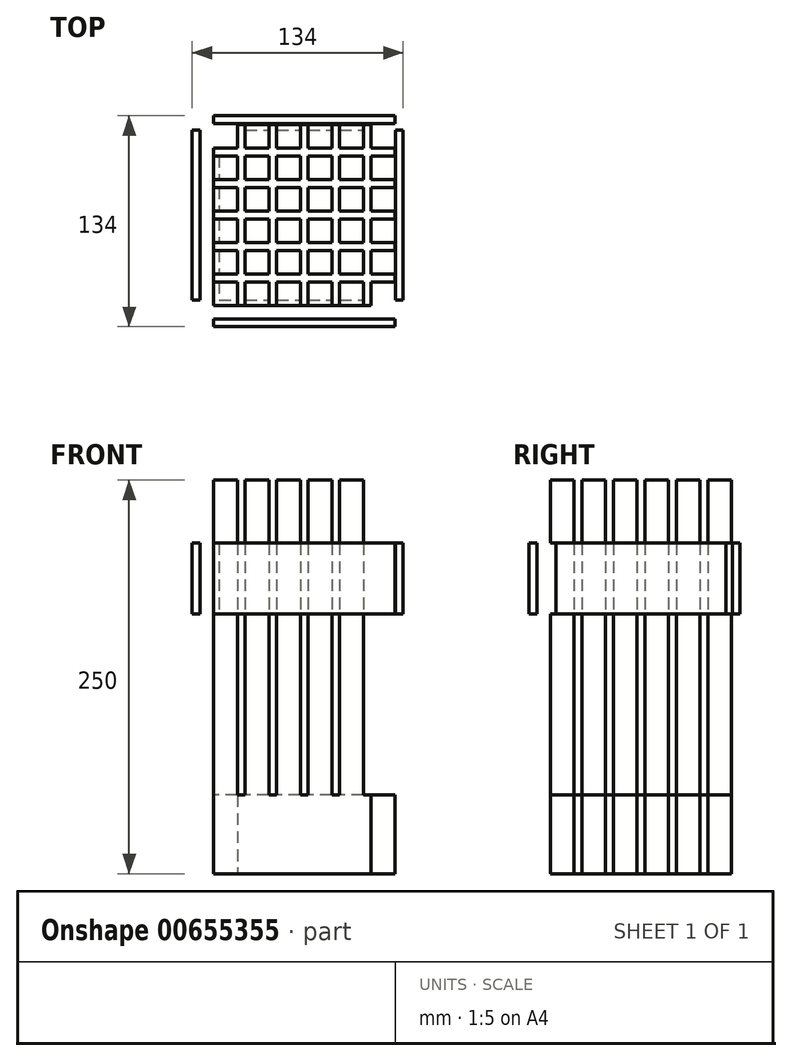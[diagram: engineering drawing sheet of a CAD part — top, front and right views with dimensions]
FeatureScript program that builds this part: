
annotation { "Feature Type Name" : "Feature", "Feature Type Description" : "" }
export const myFeature = defineFeature(function(context is Context, id is Id, definition is map)
    precondition{}
    {
        {
            var Q0;
            Q0=qCreatedBy(makeId("Top.planeOp"),FACE);
            var sketch = newSketch(context, id + "F0", { "sketchPlane" : qUnion([Q0])});
            skLineSegment(sketch, "E0.bottom", {"start": v(-53.36, 61.51) * mm, "end": v(61.64, 61.51) * mm});
            skLineSegment(sketch, "E0.top", {"start": v(-53.36, -53.49) * mm, "end": v(61.64, -53.49) * mm});
            skLineSegment(sketch, "E0.left", {"start": v(-53.36, 61.51) * mm, "end": v(-53.36, -53.49) * mm});
            skLineSegment(sketch, "E0.right", {"start": v(61.64, 61.51) * mm, "end": v(61.64, -53.49) * mm});
            skLineSegment(sketch, "E1.bottom", {"start": v(-53.36, 61.51) * mm, "end": v(-38.36, 61.51) * mm});
            skLineSegment(sketch, "E1.top", {"start": v(-53.36, 46.51) * mm, "end": v(-38.36, 46.51) * mm});
            skLineSegment(sketch, "E1.left", {"start": v(-53.36, 61.51) * mm, "end": v(-53.36, 46.51) * mm});
            skLineSegment(sketch, "E1.right", {"start": v(-38.36, 61.51) * mm, "end": v(-38.36, 46.51) * mm});
            skLineSegment(sketch, "E2.0.1.0", {"start": v(-38.36, 41.51) * mm, "end": v(-38.36, 26.51) * mm});
            skLineSegment(sketch, "E2.0.1.1", {"start": v(-53.36, 26.51) * mm, "end": v(-38.36, 26.51) * mm});
            skLineSegment(sketch, "E2.0.1.2", {"start": v(-53.36, 41.51) * mm, "end": v(-53.36, 26.51) * mm});
            skLineSegment(sketch, "E2.0.1.3", {"start": v(-53.36, 41.51) * mm, "end": v(-38.36, 41.51) * mm});
            skLineSegment(sketch, "E2.0.2.0", {"start": v(-38.36, 21.51) * mm, "end": v(-38.36, 6.51) * mm});
            skLineSegment(sketch, "E2.0.2.1", {"start": v(-53.36, 6.51) * mm, "end": v(-38.36, 6.51) * mm});
            skLineSegment(sketch, "E2.0.2.2", {"start": v(-53.36, 21.51) * mm, "end": v(-53.36, 6.51) * mm});
            skLineSegment(sketch, "E2.0.2.3", {"start": v(-53.36, 21.51) * mm, "end": v(-38.36, 21.51) * mm});
            skLineSegment(sketch, "E2.0.3.0", {"start": v(-38.36, 1.51) * mm, "end": v(-38.36, -13.49) * mm});
            skLineSegment(sketch, "E2.0.3.1", {"start": v(-53.36, -13.49) * mm, "end": v(-38.36, -13.49) * mm});
            skLineSegment(sketch, "E2.0.3.2", {"start": v(-53.36, 1.51) * mm, "end": v(-53.36, -13.49) * mm});
            skLineSegment(sketch, "E2.0.3.3", {"start": v(-53.36, 1.51) * mm, "end": v(-38.36, 1.51) * mm});
            skLineSegment(sketch, "E2.0.4.0", {"start": v(-38.36, -18.49) * mm, "end": v(-38.36, -33.49) * mm});
            skLineSegment(sketch, "E2.0.4.1", {"start": v(-53.36, -33.49) * mm, "end": v(-38.36, -33.49) * mm});
            skLineSegment(sketch, "E2.0.4.2", {"start": v(-53.36, -18.49) * mm, "end": v(-53.36, -33.49) * mm});
            skLineSegment(sketch, "E2.0.4.3", {"start": v(-53.36, -18.49) * mm, "end": v(-38.36, -18.49) * mm});
            skLineSegment(sketch, "E2.0.5.0", {"start": v(-38.36, -38.49) * mm, "end": v(-38.36, -53.49) * mm});
            skLineSegment(sketch, "E2.0.5.1", {"start": v(-53.36, -53.49) * mm, "end": v(-38.36, -53.49) * mm});
            skLineSegment(sketch, "E2.0.5.2", {"start": v(-53.36, -38.49) * mm, "end": v(-53.36, -53.49) * mm});
            skLineSegment(sketch, "E2.0.5.3", {"start": v(-53.36, -38.49) * mm, "end": v(-38.36, -38.49) * mm});
            skLineSegment(sketch, "E2.1.0.0", {"start": v(-18.36, 61.51) * mm, "end": v(-18.36, 46.51) * mm});
            skLineSegment(sketch, "E2.1.0.1", {"start": v(-33.36, 46.51) * mm, "end": v(-18.36, 46.51) * mm});
            skLineSegment(sketch, "E2.1.0.2", {"start": v(-33.36, 61.51) * mm, "end": v(-33.36, 46.51) * mm});
            skLineSegment(sketch, "E2.1.0.3", {"start": v(-33.36, 61.51) * mm, "end": v(-18.36, 61.51) * mm});
            skLineSegment(sketch, "E2.1.1.0", {"start": v(-18.36, 41.51) * mm, "end": v(-18.36, 26.51) * mm});
            skLineSegment(sketch, "E2.1.1.1", {"start": v(-33.36, 26.51) * mm, "end": v(-18.36, 26.51) * mm});
            skLineSegment(sketch, "E2.1.1.2", {"start": v(-33.36, 41.51) * mm, "end": v(-33.36, 26.51) * mm});
            skLineSegment(sketch, "E2.1.1.3", {"start": v(-33.36, 41.51) * mm, "end": v(-18.36, 41.51) * mm});
            skLineSegment(sketch, "E2.1.2.0", {"start": v(-18.36, 21.51) * mm, "end": v(-18.36, 6.51) * mm});
            skLineSegment(sketch, "E2.1.2.1", {"start": v(-33.36, 6.51) * mm, "end": v(-18.36, 6.51) * mm});
            skLineSegment(sketch, "E2.1.2.2", {"start": v(-33.36, 21.51) * mm, "end": v(-33.36, 6.51) * mm});
            skLineSegment(sketch, "E2.1.2.3", {"start": v(-33.36, 21.51) * mm, "end": v(-18.36, 21.51) * mm});
            skLineSegment(sketch, "E2.1.3.0", {"start": v(-18.36, 1.51) * mm, "end": v(-18.36, -13.49) * mm});
            skLineSegment(sketch, "E2.1.3.1", {"start": v(-33.36, -13.49) * mm, "end": v(-18.36, -13.49) * mm});
            skLineSegment(sketch, "E2.1.3.2", {"start": v(-33.36, 1.51) * mm, "end": v(-33.36, -13.49) * mm});
            skLineSegment(sketch, "E2.1.3.3", {"start": v(-33.36, 1.51) * mm, "end": v(-18.36, 1.51) * mm});
            skLineSegment(sketch, "E2.1.4.0", {"start": v(-18.36, -18.49) * mm, "end": v(-18.36, -33.49) * mm});
            skLineSegment(sketch, "E2.1.4.1", {"start": v(-33.36, -33.49) * mm, "end": v(-18.36, -33.49) * mm});
            skLineSegment(sketch, "E2.1.4.2", {"start": v(-33.36, -18.49) * mm, "end": v(-33.36, -33.49) * mm});
            skLineSegment(sketch, "E2.1.4.3", {"start": v(-33.36, -18.49) * mm, "end": v(-18.36, -18.49) * mm});
            skLineSegment(sketch, "E2.1.5.0", {"start": v(-18.36, -38.49) * mm, "end": v(-18.36, -53.49) * mm});
            skLineSegment(sketch, "E2.1.5.1", {"start": v(-33.36, -53.49) * mm, "end": v(-18.36, -53.49) * mm});
            skLineSegment(sketch, "E2.1.5.2", {"start": v(-33.36, -38.49) * mm, "end": v(-33.36, -53.49) * mm});
            skLineSegment(sketch, "E2.1.5.3", {"start": v(-33.36, -38.49) * mm, "end": v(-18.36, -38.49) * mm});
            skLineSegment(sketch, "E2.2.0.0", {"start": v(1.64, 61.51) * mm, "end": v(1.64, 46.51) * mm});
            skLineSegment(sketch, "E2.2.0.1", {"start": v(-13.36, 46.51) * mm, "end": v(1.64, 46.51) * mm});
            skLineSegment(sketch, "E2.2.0.2", {"start": v(-13.36, 61.51) * mm, "end": v(-13.36, 46.51) * mm});
            skLineSegment(sketch, "E2.2.0.3", {"start": v(-13.36, 61.51) * mm, "end": v(1.64, 61.51) * mm});
            skLineSegment(sketch, "E2.2.1.0", {"start": v(1.64, 41.51) * mm, "end": v(1.64, 26.51) * mm});
            skLineSegment(sketch, "E2.2.1.1", {"start": v(-13.36, 26.51) * mm, "end": v(1.64, 26.51) * mm});
            skLineSegment(sketch, "E2.2.1.2", {"start": v(-13.36, 41.51) * mm, "end": v(-13.36, 26.51) * mm});
            skLineSegment(sketch, "E2.2.1.3", {"start": v(-13.36, 41.51) * mm, "end": v(1.64, 41.51) * mm});
            skLineSegment(sketch, "E2.2.2.0", {"start": v(1.64, 21.51) * mm, "end": v(1.64, 6.51) * mm});
            skLineSegment(sketch, "E2.2.2.1", {"start": v(-13.36, 6.51) * mm, "end": v(1.64, 6.51) * mm});
            skLineSegment(sketch, "E2.2.2.2", {"start": v(-13.36, 21.51) * mm, "end": v(-13.36, 6.51) * mm});
            skLineSegment(sketch, "E2.2.2.3", {"start": v(-13.36, 21.51) * mm, "end": v(1.64, 21.51) * mm});
            skLineSegment(sketch, "E2.2.3.0", {"start": v(1.64, 1.51) * mm, "end": v(1.64, -13.49) * mm});
            skLineSegment(sketch, "E2.2.3.1", {"start": v(-13.36, -13.49) * mm, "end": v(1.64, -13.49) * mm});
            skLineSegment(sketch, "E2.2.3.2", {"start": v(-13.36, 1.51) * mm, "end": v(-13.36, -13.49) * mm});
            skLineSegment(sketch, "E2.2.3.3", {"start": v(-13.36, 1.51) * mm, "end": v(1.64, 1.51) * mm});
            skLineSegment(sketch, "E2.2.4.0", {"start": v(1.64, -18.49) * mm, "end": v(1.64, -33.49) * mm});
            skLineSegment(sketch, "E2.2.4.1", {"start": v(-13.36, -33.49) * mm, "end": v(1.64, -33.49) * mm});
            skLineSegment(sketch, "E2.2.4.2", {"start": v(-13.36, -18.49) * mm, "end": v(-13.36, -33.49) * mm});
            skLineSegment(sketch, "E2.2.4.3", {"start": v(-13.36, -18.49) * mm, "end": v(1.64, -18.49) * mm});
            skLineSegment(sketch, "E2.2.5.0", {"start": v(1.64, -38.49) * mm, "end": v(1.64, -53.49) * mm});
            skLineSegment(sketch, "E2.2.5.1", {"start": v(-13.36, -53.49) * mm, "end": v(1.64, -53.49) * mm});
            skLineSegment(sketch, "E2.2.5.2", {"start": v(-13.36, -38.49) * mm, "end": v(-13.36, -53.49) * mm});
            skLineSegment(sketch, "E2.2.5.3", {"start": v(-13.36, -38.49) * mm, "end": v(1.64, -38.49) * mm});
            skLineSegment(sketch, "E2.3.0.0", {"start": v(21.64, 61.51) * mm, "end": v(21.64, 46.51) * mm});
            skLineSegment(sketch, "E2.3.0.1", {"start": v(6.64, 46.51) * mm, "end": v(21.64, 46.51) * mm});
            skLineSegment(sketch, "E2.3.0.2", {"start": v(6.64, 61.51) * mm, "end": v(6.64, 46.51) * mm});
            skLineSegment(sketch, "E2.3.0.3", {"start": v(6.64, 61.51) * mm, "end": v(21.64, 61.51) * mm});
            skLineSegment(sketch, "E2.3.1.0", {"start": v(21.64, 41.51) * mm, "end": v(21.64, 26.51) * mm});
            skLineSegment(sketch, "E2.3.1.1", {"start": v(6.64, 26.51) * mm, "end": v(21.64, 26.51) * mm});
            skLineSegment(sketch, "E2.3.1.2", {"start": v(6.64, 41.51) * mm, "end": v(6.64, 26.51) * mm});
            skLineSegment(sketch, "E2.3.1.3", {"start": v(6.64, 41.51) * mm, "end": v(21.64, 41.51) * mm});
            skLineSegment(sketch, "E2.3.2.0", {"start": v(21.64, 21.51) * mm, "end": v(21.64, 6.51) * mm});
            skLineSegment(sketch, "E2.3.2.1", {"start": v(6.64, 6.51) * mm, "end": v(21.64, 6.51) * mm});
            skLineSegment(sketch, "E2.3.2.2", {"start": v(6.64, 21.51) * mm, "end": v(6.64, 6.51) * mm});
            skLineSegment(sketch, "E2.3.2.3", {"start": v(6.64, 21.51) * mm, "end": v(21.64, 21.51) * mm});
            skLineSegment(sketch, "E2.3.3.0", {"start": v(21.64, 1.51) * mm, "end": v(21.64, -13.49) * mm});
            skLineSegment(sketch, "E2.3.3.1", {"start": v(6.64, -13.49) * mm, "end": v(21.64, -13.49) * mm});
            skLineSegment(sketch, "E2.3.3.2", {"start": v(6.64, 1.51) * mm, "end": v(6.64, -13.49) * mm});
            skLineSegment(sketch, "E2.3.3.3", {"start": v(6.64, 1.51) * mm, "end": v(21.64, 1.51) * mm});
            skLineSegment(sketch, "E2.3.4.0", {"start": v(21.64, -18.49) * mm, "end": v(21.64, -33.49) * mm});
            skLineSegment(sketch, "E2.3.4.1", {"start": v(6.64, -33.49) * mm, "end": v(21.64, -33.49) * mm});
            skLineSegment(sketch, "E2.3.4.2", {"start": v(6.64, -18.49) * mm, "end": v(6.64, -33.49) * mm});
            skLineSegment(sketch, "E2.3.4.3", {"start": v(6.64, -18.49) * mm, "end": v(21.64, -18.49) * mm});
            skLineSegment(sketch, "E2.3.5.0", {"start": v(21.64, -38.49) * mm, "end": v(21.64, -53.49) * mm});
            skLineSegment(sketch, "E2.3.5.1", {"start": v(6.64, -53.49) * mm, "end": v(21.64, -53.49) * mm});
            skLineSegment(sketch, "E2.3.5.2", {"start": v(6.64, -38.49) * mm, "end": v(6.64, -53.49) * mm});
            skLineSegment(sketch, "E2.3.5.3", {"start": v(6.64, -38.49) * mm, "end": v(21.64, -38.49) * mm});
            skLineSegment(sketch, "E2.4.0.0", {"start": v(41.64, 61.51) * mm, "end": v(41.64, 46.51) * mm});
            skLineSegment(sketch, "E2.4.0.1", {"start": v(26.64, 46.51) * mm, "end": v(41.64, 46.51) * mm});
            skLineSegment(sketch, "E2.4.0.2", {"start": v(26.64, 61.51) * mm, "end": v(26.64, 46.51) * mm});
            skLineSegment(sketch, "E2.4.0.3", {"start": v(26.64, 61.51) * mm, "end": v(41.64, 61.51) * mm});
            skLineSegment(sketch, "E2.4.1.0", {"start": v(41.64, 41.51) * mm, "end": v(41.64, 26.51) * mm});
            skLineSegment(sketch, "E2.4.1.1", {"start": v(26.64, 26.51) * mm, "end": v(41.64, 26.51) * mm});
            skLineSegment(sketch, "E2.4.1.2", {"start": v(26.64, 41.51) * mm, "end": v(26.64, 26.51) * mm});
            skLineSegment(sketch, "E2.4.1.3", {"start": v(26.64, 41.51) * mm, "end": v(41.64, 41.51) * mm});
            skLineSegment(sketch, "E2.4.2.0", {"start": v(41.64, 21.51) * mm, "end": v(41.64, 6.51) * mm});
            skLineSegment(sketch, "E2.4.2.1", {"start": v(26.64, 6.51) * mm, "end": v(41.64, 6.51) * mm});
            skLineSegment(sketch, "E2.4.2.2", {"start": v(26.64, 21.51) * mm, "end": v(26.64, 6.51) * mm});
            skLineSegment(sketch, "E2.4.2.3", {"start": v(26.64, 21.51) * mm, "end": v(41.64, 21.51) * mm});
            skLineSegment(sketch, "E2.4.3.0", {"start": v(41.64, 1.51) * mm, "end": v(41.64, -13.49) * mm});
            skLineSegment(sketch, "E2.4.3.1", {"start": v(26.64, -13.49) * mm, "end": v(41.64, -13.49) * mm});
            skLineSegment(sketch, "E2.4.3.2", {"start": v(26.64, 1.51) * mm, "end": v(26.64, -13.49) * mm});
            skLineSegment(sketch, "E2.4.3.3", {"start": v(26.64, 1.51) * mm, "end": v(41.64, 1.51) * mm});
            skLineSegment(sketch, "E2.4.4.0", {"start": v(41.64, -18.49) * mm, "end": v(41.64, -33.49) * mm});
            skLineSegment(sketch, "E2.4.4.1", {"start": v(26.64, -33.49) * mm, "end": v(41.64, -33.49) * mm});
            skLineSegment(sketch, "E2.4.4.2", {"start": v(26.64, -18.49) * mm, "end": v(26.64, -33.49) * mm});
            skLineSegment(sketch, "E2.4.4.3", {"start": v(26.64, -18.49) * mm, "end": v(41.64, -18.49) * mm});
            skLineSegment(sketch, "E2.4.5.0", {"start": v(41.64, -38.49) * mm, "end": v(41.64, -53.49) * mm});
            skLineSegment(sketch, "E2.4.5.1", {"start": v(26.64, -53.49) * mm, "end": v(41.64, -53.49) * mm});
            skLineSegment(sketch, "E2.4.5.2", {"start": v(26.64, -38.49) * mm, "end": v(26.64, -53.49) * mm});
            skLineSegment(sketch, "E2.4.5.3", {"start": v(26.64, -38.49) * mm, "end": v(41.64, -38.49) * mm});
            skLineSegment(sketch, "E2.5.0.0", {"start": v(61.64, 61.51) * mm, "end": v(61.64, 46.51) * mm});
            skLineSegment(sketch, "E2.5.0.1", {"start": v(46.64, 46.51) * mm, "end": v(61.64, 46.51) * mm});
            skLineSegment(sketch, "E2.5.0.2", {"start": v(46.64, 61.51) * mm, "end": v(46.64, 46.51) * mm});
            skLineSegment(sketch, "E2.5.0.3", {"start": v(46.64, 61.51) * mm, "end": v(61.64, 61.51) * mm});
            skLineSegment(sketch, "E2.5.1.0", {"start": v(61.64, 41.51) * mm, "end": v(61.64, 26.51) * mm});
            skLineSegment(sketch, "E2.5.1.1", {"start": v(46.64, 26.51) * mm, "end": v(61.64, 26.51) * mm});
            skLineSegment(sketch, "E2.5.1.2", {"start": v(46.64, 41.51) * mm, "end": v(46.64, 26.51) * mm});
            skLineSegment(sketch, "E2.5.1.3", {"start": v(46.64, 41.51) * mm, "end": v(61.64, 41.51) * mm});
            skLineSegment(sketch, "E2.5.2.0", {"start": v(61.64, 21.51) * mm, "end": v(61.64, 6.51) * mm});
            skLineSegment(sketch, "E2.5.2.1", {"start": v(46.64, 6.51) * mm, "end": v(61.64, 6.51) * mm});
            skLineSegment(sketch, "E2.5.2.2", {"start": v(46.64, 21.51) * mm, "end": v(46.64, 6.51) * mm});
            skLineSegment(sketch, "E2.5.2.3", {"start": v(46.64, 21.51) * mm, "end": v(61.64, 21.51) * mm});
            skLineSegment(sketch, "E2.5.3.0", {"start": v(61.64, 1.51) * mm, "end": v(61.64, -13.49) * mm});
            skLineSegment(sketch, "E2.5.3.1", {"start": v(46.64, -13.49) * mm, "end": v(61.64, -13.49) * mm});
            skLineSegment(sketch, "E2.5.3.2", {"start": v(46.64, 1.51) * mm, "end": v(46.64, -13.49) * mm});
            skLineSegment(sketch, "E2.5.3.3", {"start": v(46.64, 1.51) * mm, "end": v(61.64, 1.51) * mm});
            skLineSegment(sketch, "E2.5.4.0", {"start": v(61.64, -18.49) * mm, "end": v(61.64, -33.49) * mm});
            skLineSegment(sketch, "E2.5.4.1", {"start": v(46.64, -33.49) * mm, "end": v(61.64, -33.49) * mm});
            skLineSegment(sketch, "E2.5.4.2", {"start": v(46.64, -18.49) * mm, "end": v(46.64, -33.49) * mm});
            skLineSegment(sketch, "E2.5.4.3", {"start": v(46.64, -18.49) * mm, "end": v(61.64, -18.49) * mm});
            skLineSegment(sketch, "E2.5.5.0", {"start": v(61.64, -38.49) * mm, "end": v(61.64, -53.49) * mm});
            skLineSegment(sketch, "E2.5.5.1", {"start": v(46.64, -53.49) * mm, "end": v(61.64, -53.49) * mm});
            skLineSegment(sketch, "E2.5.5.2", {"start": v(46.64, -38.49) * mm, "end": v(46.64, -53.49) * mm});
            skLineSegment(sketch, "E2.5.5.3", {"start": v(46.64, -38.49) * mm, "end": v(61.64, -38.49) * mm});
            skLineSegment(sketch, "E2.direction1", {"start": v(-38.36, 46.51) * mm, "end": v(-18.36, 46.51) * mm, "construction": true});
            skLineSegment(sketch, "E2.direction2", {"start": v(-38.36, 46.51) * mm, "end": v(-38.36, 26.51) * mm, "construction": true});
            skSolve(sketch);
        }
        {
            var Q0;
            Q0=makeQuery(id+"F0.imprint","IMPRINT",FACE,{"disambiguationData":[TD([[makeQuery(id+"F0.imprint","IMPRINT",EDGE,{"derivedFrom":sQuery(id+"F0.wireOp",EDGE,"E2.3.1.0")}),-1.0]])]});
            var Q1;
            Q1=makeQuery(id+"F0.imprint","IMPRINT",FACE,{"disambiguationData":[TD([[makeQuery(id+"F0.imprint","IMPRINT",EDGE,{"derivedFrom":sQuery(id+"F0.wireOp",EDGE,"E2.5.5.0")}),-1.0]])]});
            var Q2;
            Q2=makeQuery(id+"F0.imprint","IMPRINT",FACE,{"disambiguationData":[TD([[makeQuery(id+"F0.imprint","IMPRINT",EDGE,{"derivedFrom":sQuery(id+"F0.wireOp",EDGE,"E2.4.2.0")}),-1.0]])]});
            var Q3;
            Q3=makeQuery(id+"F0.imprint","IMPRINT",FACE,{"disambiguationData":[TD([[makeQuery(id+"F0.imprint","IMPRINT",EDGE,{"derivedFrom":sQuery(id+"F0.wireOp",EDGE,"E2.3.2.0")}),-1.0]])]});
            var Q4;
            Q4=makeQuery(id+"F0.imprint","IMPRINT",FACE,{"disambiguationData":[TD([[makeQuery(id+"F0.imprint","IMPRINT",EDGE,{"derivedFrom":sQuery(id+"F0.wireOp",EDGE,"E2.4.5.0")}),-1.0]])]});
            var Q5;
            {var subQ8=sQuery(id+"F0.wireOp",EDGE,"E1.top");Q5=makeQuery(id+"F0.imprint","IMPRINT",FACE,{"disambiguationData":[TD([[makeQuery(id+"F0.imprint","IMPRINT",EDGE,{"derivedFrom":subQ8}),-1.0]])]});}
            var Q6;
            Q6=makeQuery(id+"F0.imprint","IMPRINT",FACE,{"disambiguationData":[TD([[makeQuery(id+"F0.imprint","IMPRINT",EDGE,{"derivedFrom":sQuery(id+"F0.wireOp",EDGE,"E2.4.3.0")}),-1.0]])]});
            var Q7;
            Q7=makeQuery(id+"F0.imprint","IMPRINT",FACE,{"disambiguationData":[TD([[makeQuery(id+"F0.imprint","IMPRINT",EDGE,{"derivedFrom":sQuery(id+"F0.wireOp",EDGE,"E2.3.3.0")}),-1.0]])]});
            var Q8;
            Q8=makeQuery(id+"F0.imprint","IMPRINT",FACE,{"disambiguationData":[TD([[makeQuery(id+"F0.imprint","IMPRINT",EDGE,{"derivedFrom":sQuery(id+"F0.wireOp",EDGE,"E2.5.0.0")}),-1.0]])]});
            var Q9;
            Q9=makeQuery(id+"F0.imprint","IMPRINT",FACE,{"disambiguationData":[TD([[makeQuery(id+"F0.imprint","IMPRINT",EDGE,{"derivedFrom":sQuery(id+"F0.wireOp",EDGE,"E2.4.4.0")}),-1.0]])]});
            var Q10;
            Q10=makeQuery(id+"F0.imprint","IMPRINT",FACE,{"disambiguationData":[TD([[makeQuery(id+"F0.imprint","IMPRINT",EDGE,{"derivedFrom":sQuery(id+"F0.wireOp",EDGE,"E2.3.4.0")}),-1.0]])]});
            var Q11;
            Q11=makeQuery(id+"F0.imprint","IMPRINT",FACE,{"disambiguationData":[TD([[makeQuery(id+"F0.imprint","IMPRINT",EDGE,{"derivedFrom":sQuery(id+"F0.wireOp",EDGE,"E2.2.3.0")}),-1.0]])]});
            var Q12;
            Q12=makeQuery(id+"F0.imprint","IMPRINT",FACE,{"disambiguationData":[TD([[makeQuery(id+"F0.imprint","IMPRINT",EDGE,{"derivedFrom":sQuery(id+"F0.wireOp",EDGE,"E2.2.1.0")}),-1.0]])]});
            var Q13;
            Q13=makeQuery(id+"F0.imprint","IMPRINT",FACE,{"disambiguationData":[TD([[makeQuery(id+"F0.imprint","IMPRINT",EDGE,{"derivedFrom":sQuery(id+"F0.wireOp",EDGE,"E2.2.4.0")}),-1.0]])]});
            var Q14;
            Q14=makeQuery(id+"F0.imprint","IMPRINT",FACE,{"disambiguationData":[TD([[makeQuery(id+"F0.imprint","IMPRINT",EDGE,{"derivedFrom":sQuery(id+"F0.wireOp",EDGE,"E2.2.2.0")}),-1.0]])]});
            var Q15;
            Q15=makeQuery(id+"F0.imprint","IMPRINT",FACE,{"disambiguationData":[TD([[makeQuery(id+"F0.imprint","IMPRINT",EDGE,{"derivedFrom":sQuery(id+"F0.wireOp",EDGE,"E2.5.2.0")}),-1.0]])]});
            var Q16;
            Q16=makeQuery(id+"F0.imprint","IMPRINT",FACE,{"disambiguationData":[TD([[makeQuery(id+"F0.imprint","IMPRINT",EDGE,{"derivedFrom":sQuery(id+"F0.wireOp",EDGE,"E1.bottom")}),-1.0]])]});
            var Q17;
            Q17=makeQuery(id+"F0.imprint","IMPRINT",FACE,{"disambiguationData":[TD([[makeQuery(id+"F0.imprint","IMPRINT",EDGE,{"derivedFrom":sQuery(id+"F0.wireOp",EDGE,"E2.0.1.0")}),-1.0]])]});
            var Q18;
            Q18=makeQuery(id+"F0.imprint","IMPRINT",FACE,{"disambiguationData":[TD([[makeQuery(id+"F0.imprint","IMPRINT",EDGE,{"derivedFrom":sQuery(id+"F0.wireOp",EDGE,"E2.0.2.0")}),-1.0]])]});
            var Q19;
            Q19=makeQuery(id+"F0.imprint","IMPRINT",FACE,{"disambiguationData":[TD([[makeQuery(id+"F0.imprint","IMPRINT",EDGE,{"derivedFrom":sQuery(id+"F0.wireOp",EDGE,"E2.0.3.0")}),-1.0]])]});
            var Q20;
            Q20=makeQuery(id+"F0.imprint","IMPRINT",FACE,{"disambiguationData":[TD([[makeQuery(id+"F0.imprint","IMPRINT",EDGE,{"derivedFrom":sQuery(id+"F0.wireOp",EDGE,"E2.0.4.0")}),-1.0]])]});
            var Q21;
            Q21=makeQuery(id+"F0.imprint","IMPRINT",FACE,{"disambiguationData":[TD([[makeQuery(id+"F0.imprint","IMPRINT",EDGE,{"derivedFrom":sQuery(id+"F0.wireOp",EDGE,"E2.0.5.0")}),-1.0]])]});
            var Q22;
            Q22=makeQuery(id+"F0.imprint","IMPRINT",FACE,{"disambiguationData":[TD([[makeQuery(id+"F0.imprint","IMPRINT",EDGE,{"derivedFrom":sQuery(id+"F0.wireOp",EDGE,"E2.1.0.0")}),-1.0]])]});
            var Q23;
            Q23=makeQuery(id+"F0.imprint","IMPRINT",FACE,{"disambiguationData":[TD([[makeQuery(id+"F0.imprint","IMPRINT",EDGE,{"derivedFrom":sQuery(id+"F0.wireOp",EDGE,"E2.1.1.0")}),-1.0]])]});
            var Q24;
            Q24=makeQuery(id+"F0.imprint","IMPRINT",FACE,{"disambiguationData":[TD([[makeQuery(id+"F0.imprint","IMPRINT",EDGE,{"derivedFrom":sQuery(id+"F0.wireOp",EDGE,"E2.1.2.0")}),-1.0]])]});
            var Q25;
            Q25=makeQuery(id+"F0.imprint","IMPRINT",FACE,{"disambiguationData":[TD([[makeQuery(id+"F0.imprint","IMPRINT",EDGE,{"derivedFrom":sQuery(id+"F0.wireOp",EDGE,"E2.1.3.0")}),-1.0]])]});
            var Q26;
            Q26=makeQuery(id+"F0.imprint","IMPRINT",FACE,{"disambiguationData":[TD([[makeQuery(id+"F0.imprint","IMPRINT",EDGE,{"derivedFrom":sQuery(id+"F0.wireOp",EDGE,"E2.1.4.0")}),-1.0]])]});
            var Q27;
            Q27=makeQuery(id+"F0.imprint","IMPRINT",FACE,{"disambiguationData":[TD([[makeQuery(id+"F0.imprint","IMPRINT",EDGE,{"derivedFrom":sQuery(id+"F0.wireOp",EDGE,"E2.1.5.0")}),-1.0]])]});
            var Q28;
            Q28=makeQuery(id+"F0.imprint","IMPRINT",FACE,{"disambiguationData":[TD([[makeQuery(id+"F0.imprint","IMPRINT",EDGE,{"derivedFrom":sQuery(id+"F0.wireOp",EDGE,"E2.2.0.0")}),-1.0]])]});
            var Q29;
            Q29=makeQuery(id+"F0.imprint","IMPRINT",FACE,{"disambiguationData":[TD([[makeQuery(id+"F0.imprint","IMPRINT",EDGE,{"derivedFrom":sQuery(id+"F0.wireOp",EDGE,"E2.3.5.0")}),-1.0]])]});
            var Q30;
            Q30=makeQuery(id+"F0.imprint","IMPRINT",FACE,{"disambiguationData":[TD([[makeQuery(id+"F0.imprint","IMPRINT",EDGE,{"derivedFrom":sQuery(id+"F0.wireOp",EDGE,"E2.2.5.0")}),-1.0]])]});
            var Q31;
            Q31=makeQuery(id+"F0.imprint","IMPRINT",FACE,{"disambiguationData":[TD([[makeQuery(id+"F0.imprint","IMPRINT",EDGE,{"derivedFrom":sQuery(id+"F0.wireOp",EDGE,"E2.5.3.0")}),-1.0]])]});
            var Q32;
            Q32=makeQuery(id+"F0.imprint","IMPRINT",FACE,{"disambiguationData":[TD([[makeQuery(id+"F0.imprint","IMPRINT",EDGE,{"derivedFrom":sQuery(id+"F0.wireOp",EDGE,"E2.4.0.0")}),-1.0]])]});
            var Q33;
            Q33=makeQuery(id+"F0.imprint","IMPRINT",FACE,{"disambiguationData":[TD([[makeQuery(id+"F0.imprint","IMPRINT",EDGE,{"derivedFrom":sQuery(id+"F0.wireOp",EDGE,"E2.3.0.0")}),-1.0]])]});
            var Q34;
            Q34=makeQuery(id+"F0.imprint","IMPRINT",FACE,{"disambiguationData":[TD([[makeQuery(id+"F0.imprint","IMPRINT",EDGE,{"derivedFrom":sQuery(id+"F0.wireOp",EDGE,"E2.5.4.0")}),-1.0]])]});
            var Q35;
            Q35=makeQuery(id+"F0.imprint","IMPRINT",FACE,{"disambiguationData":[TD([[makeQuery(id+"F0.imprint","IMPRINT",EDGE,{"derivedFrom":sQuery(id+"F0.wireOp",EDGE,"E2.5.1.0")}),-1.0]])]});
            var Q36;
            Q36=makeQuery(id+"F0.imprint","IMPRINT",FACE,{"disambiguationData":[TD([[makeQuery(id+"F0.imprint","IMPRINT",EDGE,{"derivedFrom":sQuery(id+"F0.wireOp",EDGE,"E2.4.1.0")}),-1.0]])]});
            extrude(context, id + "F1", {"entities" : qUnion([Q0, Q1, Q2, Q3, Q4, Q5, Q6, Q7, Q8, Q9, Q10, Q11, Q12, Q13, Q14, Q15, Q16, Q17, Q18, Q19, Q20, Q21, Q22, Q23, Q24, Q25, Q26, Q27, Q28, Q29, Q30, Q31, Q32, Q33, Q34, Q35, Q36]), "depth" : 50 * mm, "offsetDistance" : 25 * mm});
        }
        {
            var Q0;
            Q0=makeQuery(id+"F0.imprint","IMPRINT",FACE,{"disambiguationData":[TD([[makeQuery(id+"F0.imprint","IMPRINT",EDGE,{"derivedFrom":sQuery(id+"F0.wireOp",EDGE,"E1.bottom")}),-1.0]])]});
            var Q1;
            Q1=makeQuery(id+"F0.imprint","IMPRINT",FACE,{"disambiguationData":[TD([[makeQuery(id+"F0.imprint","IMPRINT",EDGE,{"derivedFrom":sQuery(id+"F0.wireOp",EDGE,"E2.0.1.0")}),-1.0]])]});
            var Q2;
            Q2=makeQuery(id+"F0.imprint","IMPRINT",FACE,{"disambiguationData":[TD([[makeQuery(id+"F0.imprint","IMPRINT",EDGE,{"derivedFrom":sQuery(id+"F0.wireOp",EDGE,"E2.0.2.0")}),-1.0]])]});
            var Q3;
            Q3=makeQuery(id+"F0.imprint","IMPRINT",FACE,{"disambiguationData":[TD([[makeQuery(id+"F0.imprint","IMPRINT",EDGE,{"derivedFrom":sQuery(id+"F0.wireOp",EDGE,"E2.1.1.0")}),-1.0]])]});
            var Q4;
            Q4=makeQuery(id+"F0.imprint","IMPRINT",FACE,{"disambiguationData":[TD([[makeQuery(id+"F0.imprint","IMPRINT",EDGE,{"derivedFrom":sQuery(id+"F0.wireOp",EDGE,"E2.1.2.0")}),-1.0]])]});
            var Q5;
            Q5=makeQuery(id+"F0.imprint","IMPRINT",FACE,{"disambiguationData":[TD([[makeQuery(id+"F0.imprint","IMPRINT",EDGE,{"derivedFrom":sQuery(id+"F0.wireOp",EDGE,"E2.2.2.0")}),-1.0]])]});
            var Q6;
            Q6=makeQuery(id+"F0.imprint","IMPRINT",FACE,{"disambiguationData":[TD([[makeQuery(id+"F0.imprint","IMPRINT",EDGE,{"derivedFrom":sQuery(id+"F0.wireOp",EDGE,"E2.2.1.0")}),-1.0]])]});
            var Q7;
            Q7=makeQuery(id+"F0.imprint","IMPRINT",FACE,{"disambiguationData":[TD([[makeQuery(id+"F0.imprint","IMPRINT",EDGE,{"derivedFrom":sQuery(id+"F0.wireOp",EDGE,"E2.2.0.0")}),-1.0]])]});
            var Q8;
            Q8=makeQuery(id+"F0.imprint","IMPRINT",FACE,{"disambiguationData":[TD([[makeQuery(id+"F0.imprint","IMPRINT",EDGE,{"derivedFrom":sQuery(id+"F0.wireOp",EDGE,"E2.3.0.0")}),-1.0]])]});
            var Q9;
            Q9=makeQuery(id+"F0.imprint","IMPRINT",FACE,{"disambiguationData":[TD([[makeQuery(id+"F0.imprint","IMPRINT",EDGE,{"derivedFrom":sQuery(id+"F0.wireOp",EDGE,"E2.3.1.0")}),-1.0]])]});
            var Q10;
            Q10=makeQuery(id+"F0.imprint","IMPRINT",FACE,{"disambiguationData":[TD([[makeQuery(id+"F0.imprint","IMPRINT",EDGE,{"derivedFrom":sQuery(id+"F0.wireOp",EDGE,"E2.3.2.0")}),-1.0]])]});
            var Q11;
            Q11=makeQuery(id+"F0.imprint","IMPRINT",FACE,{"disambiguationData":[TD([[makeQuery(id+"F0.imprint","IMPRINT",EDGE,{"derivedFrom":sQuery(id+"F0.wireOp",EDGE,"E2.3.3.0")}),-1.0]])]});
            var Q12;
            Q12=makeQuery(id+"F0.imprint","IMPRINT",FACE,{"disambiguationData":[TD([[makeQuery(id+"F0.imprint","IMPRINT",EDGE,{"derivedFrom":sQuery(id+"F0.wireOp",EDGE,"E2.2.3.0")}),-1.0]])]});
            var Q13;
            Q13=makeQuery(id+"F0.imprint","IMPRINT",FACE,{"disambiguationData":[TD([[makeQuery(id+"F0.imprint","IMPRINT",EDGE,{"derivedFrom":sQuery(id+"F0.wireOp",EDGE,"E2.2.4.0")}),-1.0]])]});
            var Q14;
            Q14=makeQuery(id+"F0.imprint","IMPRINT",FACE,{"disambiguationData":[TD([[makeQuery(id+"F0.imprint","IMPRINT",EDGE,{"derivedFrom":sQuery(id+"F0.wireOp",EDGE,"E2.3.4.0")}),-1.0]])]});
            var Q15;
            Q15=makeQuery(id+"F0.imprint","IMPRINT",FACE,{"disambiguationData":[TD([[makeQuery(id+"F0.imprint","IMPRINT",EDGE,{"derivedFrom":sQuery(id+"F0.wireOp",EDGE,"E2.3.5.0")}),-1.0]])]});
            var Q16;
            Q16=makeQuery(id+"F0.imprint","IMPRINT",FACE,{"disambiguationData":[TD([[makeQuery(id+"F0.imprint","IMPRINT",EDGE,{"derivedFrom":sQuery(id+"F0.wireOp",EDGE,"E2.2.5.0")}),-1.0]])]});
            var Q17;
            Q17=makeQuery(id+"F0.imprint","IMPRINT",FACE,{"disambiguationData":[TD([[makeQuery(id+"F0.imprint","IMPRINT",EDGE,{"derivedFrom":sQuery(id+"F0.wireOp",EDGE,"E2.1.5.0")}),-1.0]])]});
            var Q18;
            Q18=makeQuery(id+"F0.imprint","IMPRINT",FACE,{"disambiguationData":[TD([[makeQuery(id+"F0.imprint","IMPRINT",EDGE,{"derivedFrom":sQuery(id+"F0.wireOp",EDGE,"E2.1.4.0")}),-1.0]])]});
            var Q19;
            Q19=makeQuery(id+"F0.imprint","IMPRINT",FACE,{"disambiguationData":[TD([[makeQuery(id+"F0.imprint","IMPRINT",EDGE,{"derivedFrom":sQuery(id+"F0.wireOp",EDGE,"E2.1.3.0")}),-1.0]])]});
            var Q20;
            Q20=makeQuery(id+"F0.imprint","IMPRINT",FACE,{"disambiguationData":[TD([[makeQuery(id+"F0.imprint","IMPRINT",EDGE,{"derivedFrom":sQuery(id+"F0.wireOp",EDGE,"E2.0.3.0")}),-1.0]])]});
            var Q21;
            Q21=makeQuery(id+"F0.imprint","IMPRINT",FACE,{"disambiguationData":[TD([[makeQuery(id+"F0.imprint","IMPRINT",EDGE,{"derivedFrom":sQuery(id+"F0.wireOp",EDGE,"E2.0.4.0")}),-1.0]])]});
            var Q22;
            Q22=makeQuery(id+"F0.imprint","IMPRINT",FACE,{"disambiguationData":[TD([[makeQuery(id+"F0.imprint","IMPRINT",EDGE,{"derivedFrom":sQuery(id+"F0.wireOp",EDGE,"E2.0.5.0")}),-1.0]])]});
            var Q23;
            Q23=makeQuery(id+"F0.imprint","IMPRINT",FACE,{"disambiguationData":[TD([[makeQuery(id+"F0.imprint","IMPRINT",EDGE,{"derivedFrom":sQuery(id+"F0.wireOp",EDGE,"E2.1.0.0")}),-1.0]])]});
            var Q24;
            Q24=makeQuery(id+"F0.imprint","IMPRINT",FACE,{"disambiguationData":[TD([[makeQuery(id+"F0.imprint","IMPRINT",EDGE,{"derivedFrom":sQuery(id+"F0.wireOp",EDGE,"E2.4.0.0")}),-1.0]])]});
            var Q25;
            Q25=makeQuery(id+"F0.imprint","IMPRINT",FACE,{"disambiguationData":[TD([[makeQuery(id+"F0.imprint","IMPRINT",EDGE,{"derivedFrom":sQuery(id+"F0.wireOp",EDGE,"E2.5.0.0")}),-1.0]])]});
            var Q26;
            Q26=makeQuery(id+"F0.imprint","IMPRINT",FACE,{"disambiguationData":[TD([[makeQuery(id+"F0.imprint","IMPRINT",EDGE,{"derivedFrom":sQuery(id+"F0.wireOp",EDGE,"E2.4.1.0")}),-1.0]])]});
            var Q27;
            Q27=makeQuery(id+"F0.imprint","IMPRINT",FACE,{"disambiguationData":[TD([[makeQuery(id+"F0.imprint","IMPRINT",EDGE,{"derivedFrom":sQuery(id+"F0.wireOp",EDGE,"E2.4.2.0")}),-1.0]])]});
            var Q28;
            Q28=makeQuery(id+"F0.imprint","IMPRINT",FACE,{"disambiguationData":[TD([[makeQuery(id+"F0.imprint","IMPRINT",EDGE,{"derivedFrom":sQuery(id+"F0.wireOp",EDGE,"E2.5.2.0")}),-1.0]])]});
            var Q29;
            Q29=makeQuery(id+"F0.imprint","IMPRINT",FACE,{"disambiguationData":[TD([[makeQuery(id+"F0.imprint","IMPRINT",EDGE,{"derivedFrom":sQuery(id+"F0.wireOp",EDGE,"E2.5.1.0")}),-1.0]])]});
            var Q30;
            Q30=makeQuery(id+"F0.imprint","IMPRINT",FACE,{"disambiguationData":[TD([[makeQuery(id+"F0.imprint","IMPRINT",EDGE,{"derivedFrom":sQuery(id+"F0.wireOp",EDGE,"E2.4.3.0")}),-1.0]])]});
            var Q31;
            Q31=makeQuery(id+"F0.imprint","IMPRINT",FACE,{"disambiguationData":[TD([[makeQuery(id+"F0.imprint","IMPRINT",EDGE,{"derivedFrom":sQuery(id+"F0.wireOp",EDGE,"E2.5.4.0")}),-1.0]])]});
            var Q32;
            Q32=makeQuery(id+"F0.imprint","IMPRINT",FACE,{"disambiguationData":[TD([[makeQuery(id+"F0.imprint","IMPRINT",EDGE,{"derivedFrom":sQuery(id+"F0.wireOp",EDGE,"E2.4.5.0")}),-1.0]])]});
            var Q33;
            Q33=makeQuery(id+"F0.imprint","IMPRINT",FACE,{"disambiguationData":[TD([[makeQuery(id+"F0.imprint","IMPRINT",EDGE,{"derivedFrom":sQuery(id+"F0.wireOp",EDGE,"E2.4.4.0")}),-1.0]])]});
            var Q34;
            Q34=makeQuery(id+"F0.imprint","IMPRINT",FACE,{"disambiguationData":[TD([[makeQuery(id+"F0.imprint","IMPRINT",EDGE,{"derivedFrom":sQuery(id+"F0.wireOp",EDGE,"E2.5.3.0")}),-1.0]])]});
            var Q35;
            Q35=makeQuery(id+"F0.imprint","IMPRINT",FACE,{"disambiguationData":[TD([[makeQuery(id+"F0.imprint","IMPRINT",EDGE,{"derivedFrom":sQuery(id+"F0.wireOp",EDGE,"E2.5.5.0")}),-1.0]])]});
            extrude(context, id + "F2", {"entities" : qUnion([Q0, Q1, Q2, Q3, Q4, Q5, Q6, Q7, Q8, Q9, Q10, Q11, Q12, Q13, Q14, Q15, Q16, Q17, Q18, Q19, Q20, Q21, Q22, Q23, Q24, Q25, Q26, Q27, Q28, Q29, Q30, Q31, Q32, Q33, Q34, Q35]), "operationType" : NewBodyOperationType.ADD, "depth" : 250 * mm, "offsetDistance" : 25 * mm});
        }
        {
            var Q0;
            Q0=qCreatedBy(makeId("Front.planeOp"),FACE);
            var sketch = newSketch(context, id + "F3", { "sketchPlane" : qUnion([Q0])});
            skLineSegment(sketch, "E3.bottom", {"start": v(-53.36, 210) * mm, "end": v(61.64, 210) * mm});
            skLineSegment(sketch, "E3.top", {"start": v(-53.36, 165) * mm, "end": v(61.64, 165) * mm});
            skLineSegment(sketch, "E3.left", {"start": v(-53.36, 210) * mm, "end": v(-53.36, 165) * mm});
            skLineSegment(sketch, "E3.right", {"start": v(61.64, 210) * mm, "end": v(61.64, 165) * mm});
            skSolve(sketch);
        }
        {
            var Q0;
            Q0=makeQuery(id+"F3.imprint","IMPRINT",FACE,{"disambiguationData":[TD([[makeQuery(id+"F3.imprint","IMPRINT",EDGE,{"derivedFrom":sQuery(id+"F3.wireOp",EDGE,"E3.bottom")}),-1.0]])]});
            extrude(context, id + "F4", {"entities" : qUnion([Q0]), "operationType" : NewBodyOperationType.REMOVE, "depth" : 55 * mm, "offsetDistance" : 25 * mm, "hasSecondDirection" : true, "secondDirectionOppositeDirection" : false, "secondDirectionDepth" : 50 * mm});
        }
        {
            var Q0;
            Q0 = qSketchRegion(id + "F3", true);
            extrude(context, id + "F5", {"entities" : qUnion([Q0]), "operationType" : NewBodyOperationType.REMOVE, "oppositeDirection" : true, "depth" : 65 * mm, "offsetDistance" : 25 * mm, "hasSecondDirection" : true, "secondDirectionOppositeDirection" : true, "secondDirectionDepth" : 58 * mm});
        }
        {
            var Q0;
            Q0 = qSketchRegion(id + "F3", true);
            extrude(context, id + "F6", {"entities" : qUnion([Q0]), "depth" : 67 * mm, "offsetDistance" : 25 * mm, "hasSecondDirection" : true, "secondDirectionOppositeDirection" : false, "secondDirectionDepth" : 62 * mm});
        }
        {
            var Q0;
            Q0=makeQuery(id+"F6.opExtrude","SWEPT_BODY",BODY,{"disambiguationData":[OSD([sQuery(id+"F3.wireOp",EDGE,"E3.bottom"),sQuery(id+"F3.wireOp",EDGE,"E3.top"),sQuery(id+"F3.wireOp",EDGE,"E3.left"),sQuery(id+"F3.wireOp",EDGE,"E3.right")])]});
            var Q1;
            Q1=qCreatedBy(makeId("Front.planeOp"),FACE);
            mirror(context, id + "F7", {"entities" : qUnion([Q0]), "mirrorPlane" : qUnion([Q1])});
        }
        {
            var Q0;
            Q0=qCreatedBy(makeId("Right.planeOp"),FACE);
            var sketch = newSketch(context, id + "F8", { "sketchPlane" : qUnion([Q0])});
            skLineSegment(sketch, "E4.bottom", {"start": v(58, 210) * mm, "end": v(-50, 210) * mm});
            skLineSegment(sketch, "E4.top", {"start": v(58, 165) * mm, "end": v(-50, 165) * mm});
            skLineSegment(sketch, "E4.left", {"start": v(58, 210) * mm, "end": v(58, 165) * mm});
            skLineSegment(sketch, "E4.right", {"start": v(-50, 210) * mm, "end": v(-50, 165) * mm});
            skSolve(sketch);
        }
        {
            var Q0;
            Q0=makeQuery(id+"F8.imprint","IMPRINT",FACE,{"disambiguationData":[TD([[makeQuery(id+"F8.imprint","IMPRINT",EDGE,{"derivedFrom":sQuery(id+"F8.wireOp",EDGE,"E4.bottom")}),1.0]])]});
            extrude(context, id + "F9", {"entities" : qUnion([Q0]), "operationType" : NewBodyOperationType.REMOVE, "oppositeDirection" : true, "depth" : 55 * mm, "offsetDistance" : 25 * mm, "hasSecondDirection" : true, "secondDirectionOppositeDirection" : true, "secondDirectionDepth" : 50 * mm});
        }
        {
            var Q0;
            Q0 = qSketchRegion(id + "F8", true);
            extrude(context, id + "F10", {"entities" : qUnion([Q0]), "operationType" : NewBodyOperationType.REMOVE, "depth" : 65 * mm, "offsetDistance" : 25 * mm, "hasSecondDirection" : true, "secondDirectionOppositeDirection" : false, "secondDirectionDepth" : 60 * mm});
        }
        {
            var Q0;
            Q0 = qSketchRegion(id + "F8", true);
            extrude(context, id + "F11", {"entities" : qUnion([Q0]), "oppositeDirection" : true, "depth" : 67 * mm, "offsetDistance" : 25 * mm, "hasSecondDirection" : true, "secondDirectionOppositeDirection" : true, "secondDirectionDepth" : 62 * mm});
        }
        {
            var Q0;
            Q0=makeQuery(id+"F11.opExtrude","SWEPT_BODY",BODY,{"disambiguationData":[OSD([sQuery(id+"F8.wireOp",EDGE,"E4.bottom"),sQuery(id+"F8.wireOp",EDGE,"E4.top"),sQuery(id+"F8.wireOp",EDGE,"E4.left"),sQuery(id+"F8.wireOp",EDGE,"E4.right")])]});
            var Q1;
            Q1=qCreatedBy(makeId("Right.planeOp"),FACE);
            mirror(context, id + "F12", {"entities" : qUnion([Q0]), "mirrorPlane" : qUnion([Q1])});
        }
    });
